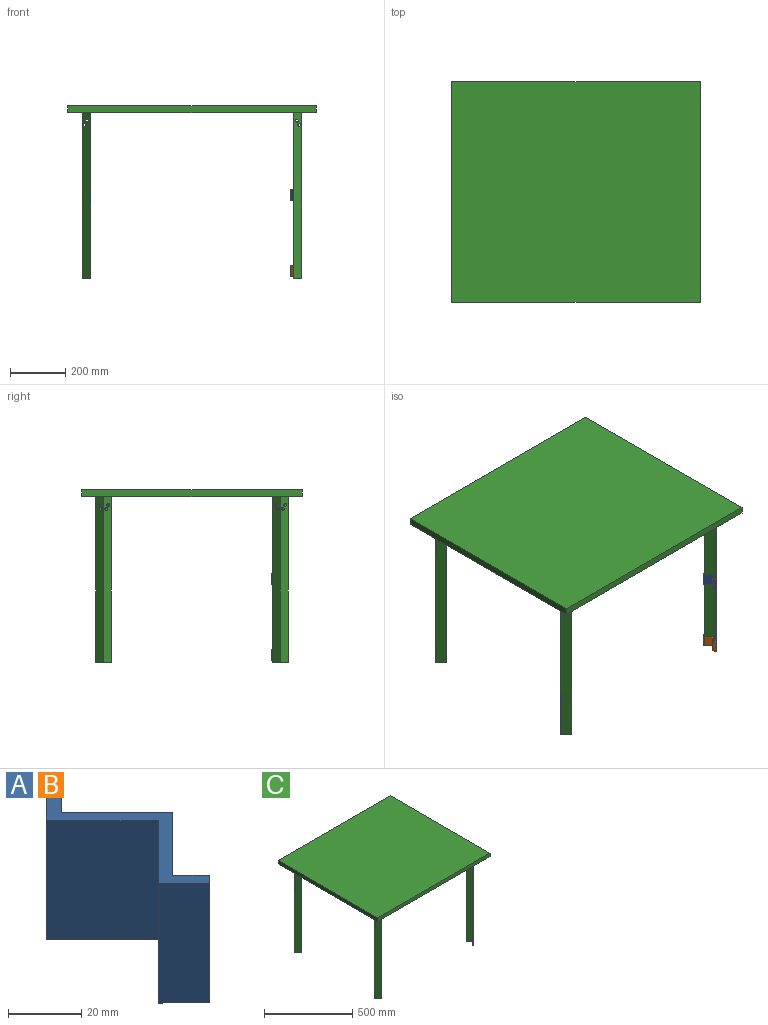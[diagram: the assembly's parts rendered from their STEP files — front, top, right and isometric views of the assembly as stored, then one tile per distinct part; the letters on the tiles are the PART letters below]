
ASSEMBLY  parts=3 mates=2
PART A: 12 faces, bbox 27.2x62.6x40 mm
  f0: plane 40x7.07mm, normal (0.71,-0.71,0), area 400mm2, adj f1,f2,f3,f11
  f1: plane 62.58x27.22mm, normal (0,0,1), area 338mm2, adj f0,f2,f4,f5,f6,f7,f8,f9
  f2: plane 40x2.83mm, normal (0.71,0.71,0), area 160mm2, adj f0,f1,f3,f4
  f3: plane 62.58x27.22mm, normal (0,0,-1), area 338mm2, adj f0,f2,f4,f5,f6,f7,f8,f9
  f4: plane 40x9.9mm, normal (-0.71,0.71,0), area 560mm2, adj f1,f2,f3,f5
  f5: plane 40x21.57mm, normal (-0.71,-0.71,0), area 1220mm2, adj f1,f3,f4,f7
  f6: plane 40x21.21mm, normal (0.71,-0.71,0), area 1200mm2, adj f1,f3,f9,f11
  f7: plane 40x21.21mm, normal (-0.71,0.71,0), area 1200mm2, adj f1,f3,f5,f8
  f8: plane 40x9.9mm, normal (-0.71,-0.71,0), area 560mm2, adj f1,f3,f7,f10
  f9: plane 40x7.07mm, normal (0.71,0.71,0), area 400mm2, adj f1,f3,f6,f10
  f10: plane 40x2.83mm, normal (0.71,-0.71,0), area 160mm2, adj f1,f3,f8,f9
  f11: plane 40x21.57mm, normal (0.71,0.71,0), area 1220mm2, adj f0,f1,f3,f6
PART B: same geometry as A
PART C: 46 faces, bbox 902.1x802.1x627.1 mm
  f0: plane 900x800mm, normal (0,0,-1), area 718784mm2, adj f1,f2,f3,f4,f6,f7,f8,f9
  f1: plane 800x25mm, normal (1,0,0), area 20000mm2, adj f0,f2,f4,f5
  f2: plane 900x25mm, normal (0,1,0), area 22500mm2, adj f0,f1,f3,f5
  f3: plane 800x25mm, normal (-1,0,0), area 20000mm2, adj f0,f2,f4,f5
  f4: plane 900x25mm, normal (0,-1,0), area 22500mm2, adj f0,f1,f3,f5
  f5: plane 900x800mm, normal (0,0,1), area 720000mm2, adj f1,f2,f3,f4
  f6: plane 600x28.28mm, normal (0.71,0.71,0), area 23777.9mm2, adj f0,f7,f11,f12,f13,f15
  f7: plane 600x2.83mm, normal (-0.71,0.71,0), area 2400mm2, adj f0,f6,f8,f12
  f8: plane 600x25.46mm, normal (-0.71,-0.71,0), area 21384.4mm2, adj f0,f7,f9,f12,f13,f15
  f9: plane 600x25.46mm, normal (-0.71,0.71,0), area 21384.4mm2, adj f0,f8,f10,f12,f13,f14
  f10: plane 600x2.83mm, normal (-0.71,-0.71,0), area 2400mm2, adj f0,f9,f11,f12
  f11: plane 602.1x30.39mm, normal (0.71,-0.71,0), area 23777.9mm2, adj f0,f6,f10,f12,f13,f14
  f12: plane 56.57x31.11mm, normal (0,0,-1), area 304mm2, adj f6,f7,f8,f9,f10,f11
  f13: cylinder r=5mm len=29.21mm, axis (0,-1,0), area 345.8mm2, adj f6,f8,f9,f11
  f14: cylinder r=5mm len=15.73mm, axis (0,-1,0), area 177.7mm2, adj f9,f11
  f15: cylinder r=5mm len=15.73mm, axis (0,-1,0), area 177.7mm2, adj f6,f8
  f16: plane 600x28.28mm, normal (0.71,0.71,0), area 23777.9mm2, adj f0,f17,f21,f22,f23,f25
  f17: plane 600x2.83mm, normal (-0.71,0.71,0), area 2400mm2, adj f0,f16,f18,f22
  f18: plane 600x25.46mm, normal (-0.71,-0.71,0), area 21384.4mm2, adj f0,f17,f19,f22,f23,f25
  f19: plane 600x25.46mm, normal (-0.71,0.71,0), area 21384.4mm2, adj f0,f18,f20,f22,f23,f24
  f20: plane 600x2.83mm, normal (-0.71,-0.71,0), area 2400mm2, adj f0,f19,f21,f22
  f21: plane 602.1x30.39mm, normal (0.71,-0.71,0), area 23777.9mm2, adj f0,f16,f20,f22,f23,f24
  f22: plane 56.57x31.11mm, normal (0,0,-1), area 304mm2, adj f16,f17,f18,f19,f20,f21
  f23: cylinder r=5mm len=29.21mm, axis (0,-1,0), area 345.8mm2, adj f16,f18,f19,f21
  f24: cylinder r=5mm len=15.73mm, axis (0,-1,0), area 177.7mm2, adj f19,f21
  f25: cylinder r=5mm len=15.73mm, axis (0,-1,0), area 177.7mm2, adj f16,f18
  f26: plane 600x28.28mm, normal (-0.71,0.71,0), area 23777.9mm2, adj f0,f27,f31,f32,f33,f35
  f27: plane 600x2.83mm, normal (0.71,0.71,0), area 2400mm2, adj f0,f26,f28,f32
  f28: plane 600x25.46mm, normal (0.71,-0.71,0), area 21384.4mm2, adj f0,f27,f29,f32,f33,f35
  f29: plane 600x25.46mm, normal (0.71,0.71,0), area 21384.4mm2, adj f0,f28,f30,f32,f33,f34
  f30: plane 600x2.83mm, normal (0.71,-0.71,0), area 2400mm2, adj f0,f29,f31,f32
  f31: plane 602.1x30.39mm, normal (-0.71,-0.71,0), area 23777.9mm2, adj f0,f26,f30,f32,f33,f34
  f32: plane 56.57x31.11mm, normal (0,0,-1), area 304mm2, adj f26,f27,f28,f29,f30,f31
  f33: cylinder r=5mm len=29.21mm, axis (0,-1,0), area 345.8mm2, adj f26,f28,f29,f31
  f34: cylinder r=5mm len=15.73mm, axis (0,-1,0), area 177.7mm2, adj f29,f31
  f35: cylinder r=5mm len=15.73mm, axis (0,-1,0), area 177.7mm2, adj f26,f28
  f36: plane 600x28.28mm, normal (-0.71,0.71,0), area 23777.9mm2, adj f0,f37,f41,f42,f43,f45
  f37: plane 600x2.83mm, normal (0.71,0.71,0), area 2400mm2, adj f0,f36,f38,f42
  f38: plane 600x25.46mm, normal (0.71,-0.71,0), area 21384.4mm2, adj f0,f37,f39,f42,f43,f45
  f39: plane 600x25.46mm, normal (0.71,0.71,0), area 21384.4mm2, adj f0,f38,f40,f42,f43,f44
  f40: plane 600x2.83mm, normal (0.71,-0.71,0), area 2400mm2, adj f0,f39,f41,f42
  f41: plane 602.1x30.39mm, normal (-0.71,-0.71,0), area 23777.9mm2, adj f0,f36,f40,f42,f43,f44
  f42: plane 56.57x31.11mm, normal (0,0,-1), area 304mm2, adj f36,f37,f38,f39,f40,f41
  f43: cylinder r=5mm len=29.21mm, axis (0,-1,0), area 345.8mm2, adj f36,f38,f39,f41
  f44: cylinder r=5mm len=15.73mm, axis (0,-1,0), area 177.7mm2, adj f39,f41
  f45: cylinder r=5mm len=15.73mm, axis (0,-1,0), area 177.7mm2, adj f36,f38
PLACE A t=(75.65,-223.75,-6.57)mm
PLACE B t=(75.65,-223.75,-279.57)mm
PLACE C t=(76.01,-224.1,107.3)mm
MATE planar B.f9 <-> C.f10  axis (0.71,0.71,0) through (862.83,-183.06,-465.7)mm
MATE planar A.f9 <-> C.f10  axis (0.71,0.71,0) through (862.83,-183.06,-192.7)mm
